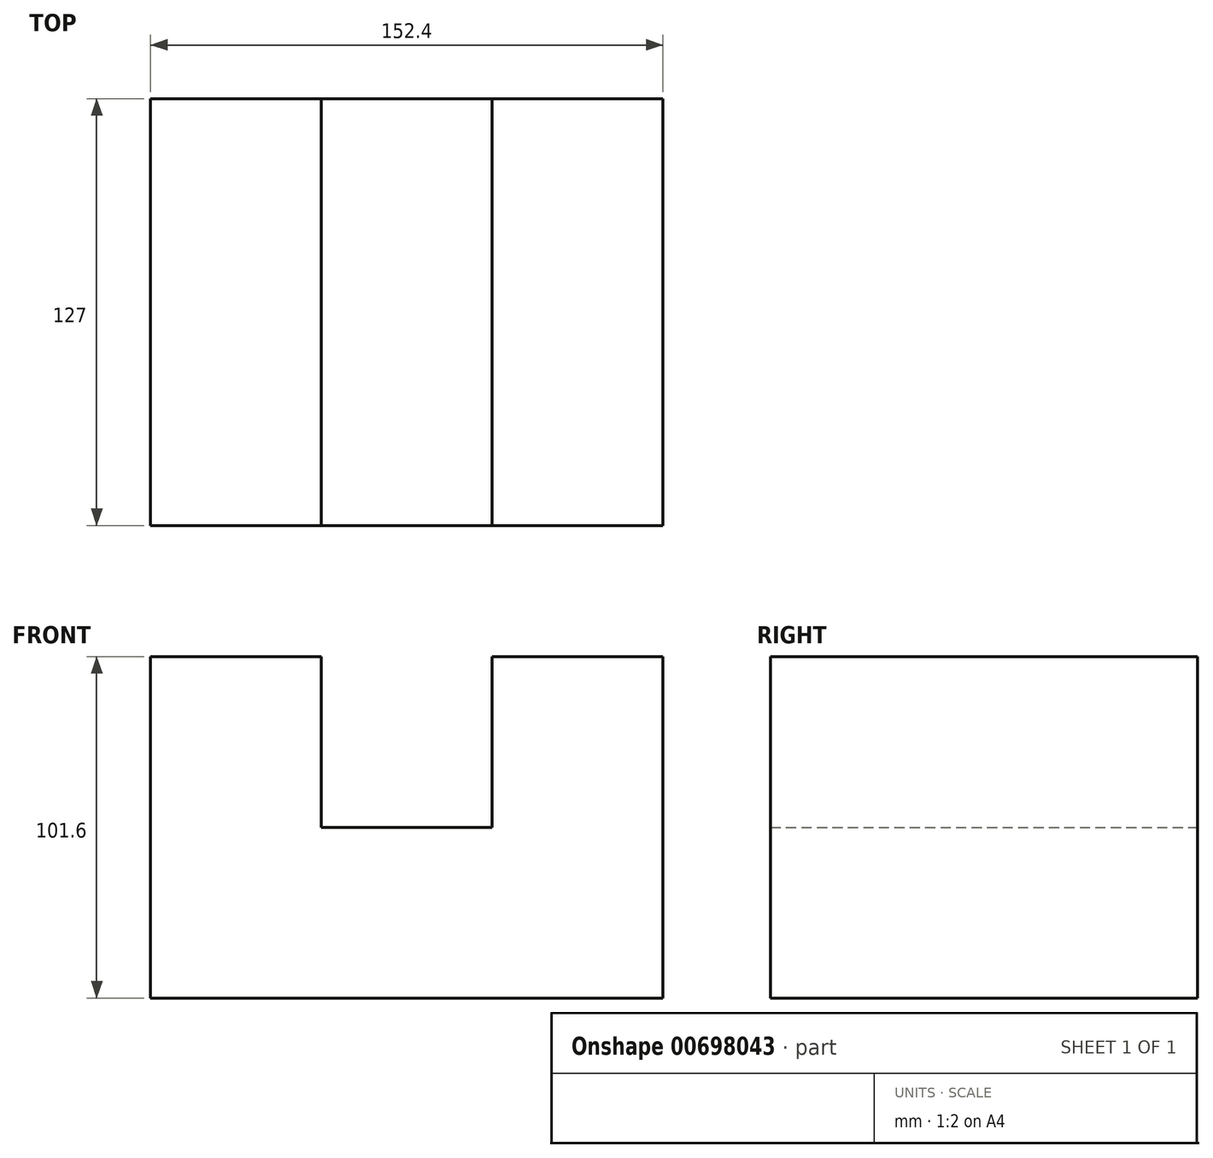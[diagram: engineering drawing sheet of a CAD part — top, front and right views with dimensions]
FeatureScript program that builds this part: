
annotation { "Feature Type Name" : "Feature", "Feature Type Description" : "" }
export const myFeature = defineFeature(function(context is Context, id is Id, definition is map)
    precondition{}
    {
        {
            var Q0;
            Q0=qCreatedBy(makeId("Front.planeOp"),FACE);
            var sketch = newSketch(context, id + "F0", { "sketchPlane" : qUnion([Q0])});
            skLineSegment(sketch, "E0", {"start": v(-63.66, -11.76) * mm, "end": v(88.74, -11.76) * mm});
            skLineSegment(sketch, "E1", {"start": v(88.74, -11.76) * mm, "end": v(88.74, 89.84) * mm});
            skLineSegment(sketch, "E2", {"start": v(88.74, 89.84) * mm, "end": v(37.94, 89.84) * mm});
            skLineSegment(sketch, "E3", {"start": v(37.94, 89.84) * mm, "end": v(37.94, 39.04) * mm});
            skLineSegment(sketch, "E4", {"start": v(37.94, 39.04) * mm, "end": v(-12.86, 39.04) * mm});
            skLineSegment(sketch, "E5", {"start": v(-12.86, 39.04) * mm, "end": v(-12.86, 89.84) * mm});
            skLineSegment(sketch, "E6", {"start": v(-12.86, 89.84) * mm, "end": v(-63.66, 89.84) * mm});
            skLineSegment(sketch, "E7", {"start": v(-63.66, 89.84) * mm, "end": v(-63.66, -11.76) * mm});
            skSolve(sketch);
        }
        {
            var Q0;
            Q0=makeQuery(id+"F0.imprint","IMPRINT",FACE,{"disambiguationData":[TD([[makeQuery(id+"F0.imprint","IMPRINT",EDGE,{"derivedFrom":sQuery(id+"F0.wireOp",EDGE,"E0")}),1.0]])]});
            extrude(context, id + "F1", {"entities" : qUnion([Q0]), "depth" : 127 * mm, "offsetDistance" : 25.4 * mm});
        }
    });
